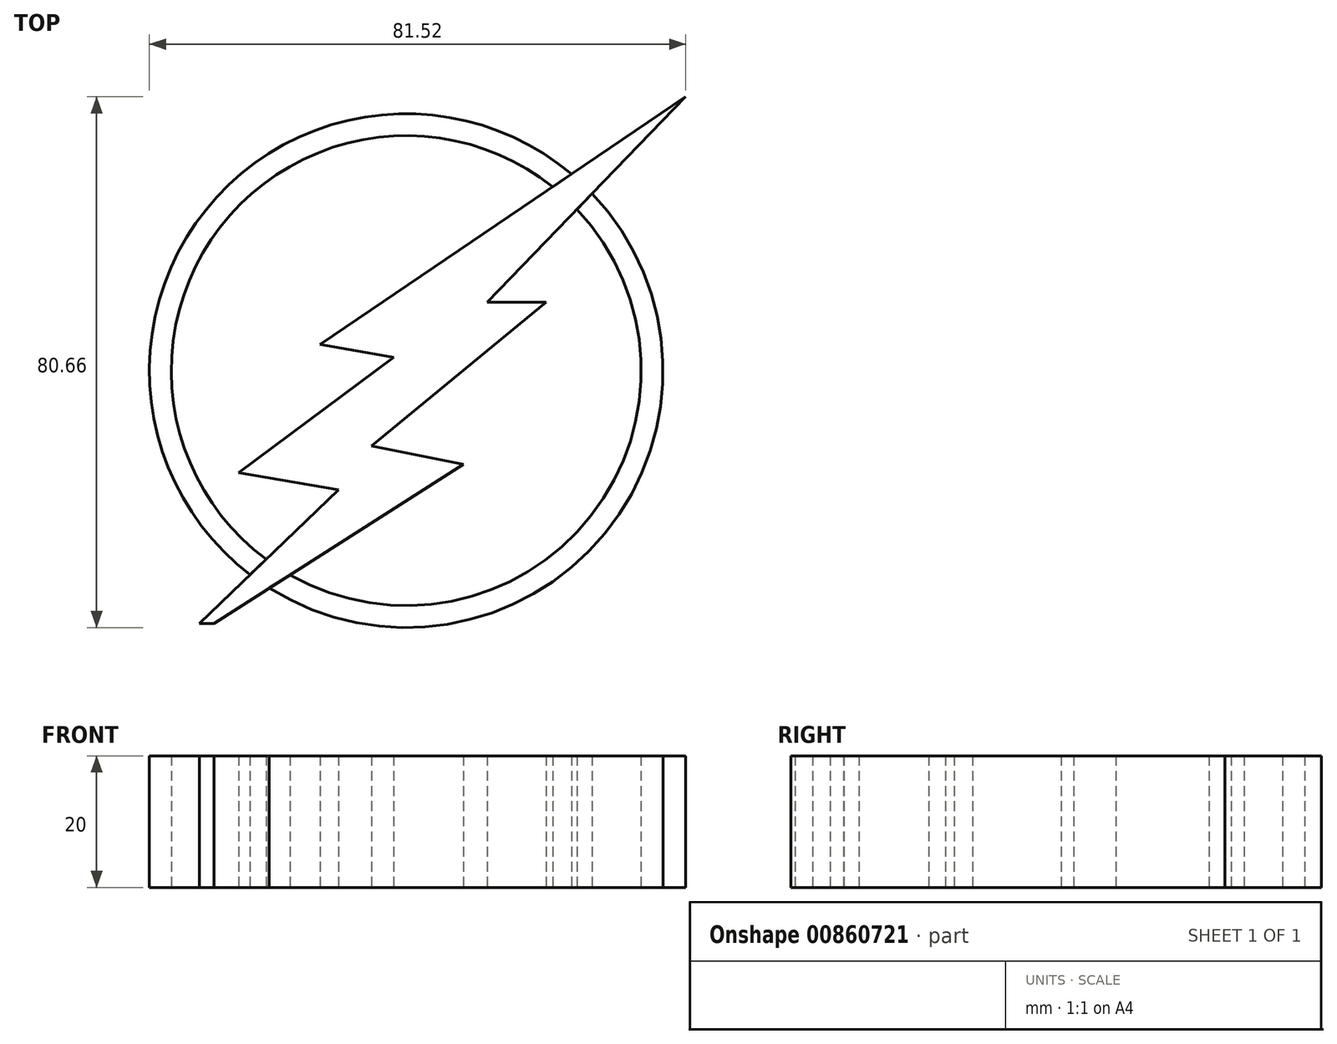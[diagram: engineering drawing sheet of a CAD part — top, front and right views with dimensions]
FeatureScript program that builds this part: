
annotation { "Feature Type Name" : "Feature", "Feature Type Description" : "" }
export const myFeature = defineFeature(function(context is Context, id is Id, definition is map)
    precondition{}
    {
        {
            var Q0;
            Q0=qCreatedBy(makeId("Top.planeOp"),FACE);
            var sketch = newSketch(context, id + "F0", { "sketchPlane" : qUnion([Q0])});
            skArc(sketch, "E0", {"start": v(22.27, 27.92) * mm, "mid": v(-28.3, 21.8) * mm, "end": v(-21.3, -28.66) * mm});
            skLineSegment(sketch, "E1", {"start": v(42.48, 41.62) * mm, "end": v(12.3, 10.38) * mm});
            skLineSegment(sketch, "E2", {"start": v(12.3, 10.38) * mm, "end": v(21.3, 10.38) * mm});
            skLineSegment(sketch, "E3", {"start": v(21.3, 10.38) * mm, "end": v(-5.24, -11.45) * mm});
            skLineSegment(sketch, "E4", {"start": v(-5.24, -11.45) * mm, "end": v(8.67, -14.23) * mm});
            skLineSegment(sketch, "E5", {"start": v(8.67, -14.23) * mm, "end": v(-29.21, -38.41) * mm});
            skLineSegment(sketch, "E6", {"start": v(42.48, 41.62) * mm, "end": v(-13.06, 3.96) * mm});
            skLineSegment(sketch, "E7", {"start": v(-13.06, 3.96) * mm, "end": v(-1.93, 2.03) * mm});
            skLineSegment(sketch, "E8", {"start": v(-1.93, 2.03) * mm, "end": v(-25.47, -15.51) * mm});
            skLineSegment(sketch, "E9", {"start": v(-25.47, -15.51) * mm, "end": v(-10.27, -18.08) * mm});
            skLineSegment(sketch, "E10", {"start": v(-10.27, -18.08) * mm, "end": v(-31.46, -38.41) * mm});
            skLineSegment(sketch, "E11", {"start": v(-31.46, -38.41) * mm, "end": v(-29.21, -38.41) * mm});
            skArc(sketch, "E12", {"start": v(25.15, 29.87) * mm, "mid": v(-30.44, 24.45) * mm, "end": v(-23.74, -31) * mm});
            skArc(sketch, "E13.trimOffspring", {"start": v(-17.66, -31.04) * mm, "mid": v(28.09, -22.06) * mm, "end": v(25.96, 24.52) * mm});
            skArc(sketch, "E14.trimOffspring", {"start": v(-20.8, -33.04) * mm, "mid": v(30.21, -24.73) * mm, "end": v(28.28, 26.92) * mm});
            skSolve(sketch);
        }
        {
            var Q0;
            {var subQ0=sQuery(id+"F0.wireOp",EDGE,"E0");Q0=makeQuery(id+"F0.imprint","IMPRINT",FACE,{"disambiguationData":[TD([[makeQuery(id+"F0.imprint","IMPRINT",EDGE,{"derivedFrom":subQ0}),-1.0]])]});}
            var Q1;
            {var subQ0=sQuery(id+"F0.wireOp",EDGE,"E13.trimOffspring");Q1=makeQuery(id+"F0.imprint","IMPRINT",FACE,{"disambiguationData":[TD([[makeQuery(id+"F0.imprint","IMPRINT",EDGE,{"derivedFrom":subQ0}),-1.0]])]});}
            extrude(context, id + "F1", {"entities" : qUnion([Q0, Q1]), "depth" : 20 * mm, "offsetDistance" : 25 * mm});
        }
        {
            var Q0;
            {var subQ14=sQuery(id+"F0.wireOp",EDGE,"E2");Q0=makeQuery(id+"F0.imprint","IMPRINT",FACE,{"disambiguationData":[TD([[makeQuery(id+"F0.imprint","IMPRINT",EDGE,{"derivedFrom":subQ14}),-1.0]])]});}
            extrude(context, id + "F2", {"entities" : qUnion([Q0]), "depth" : 20 * mm, "offsetDistance" : 25 * mm});
        }
    });
